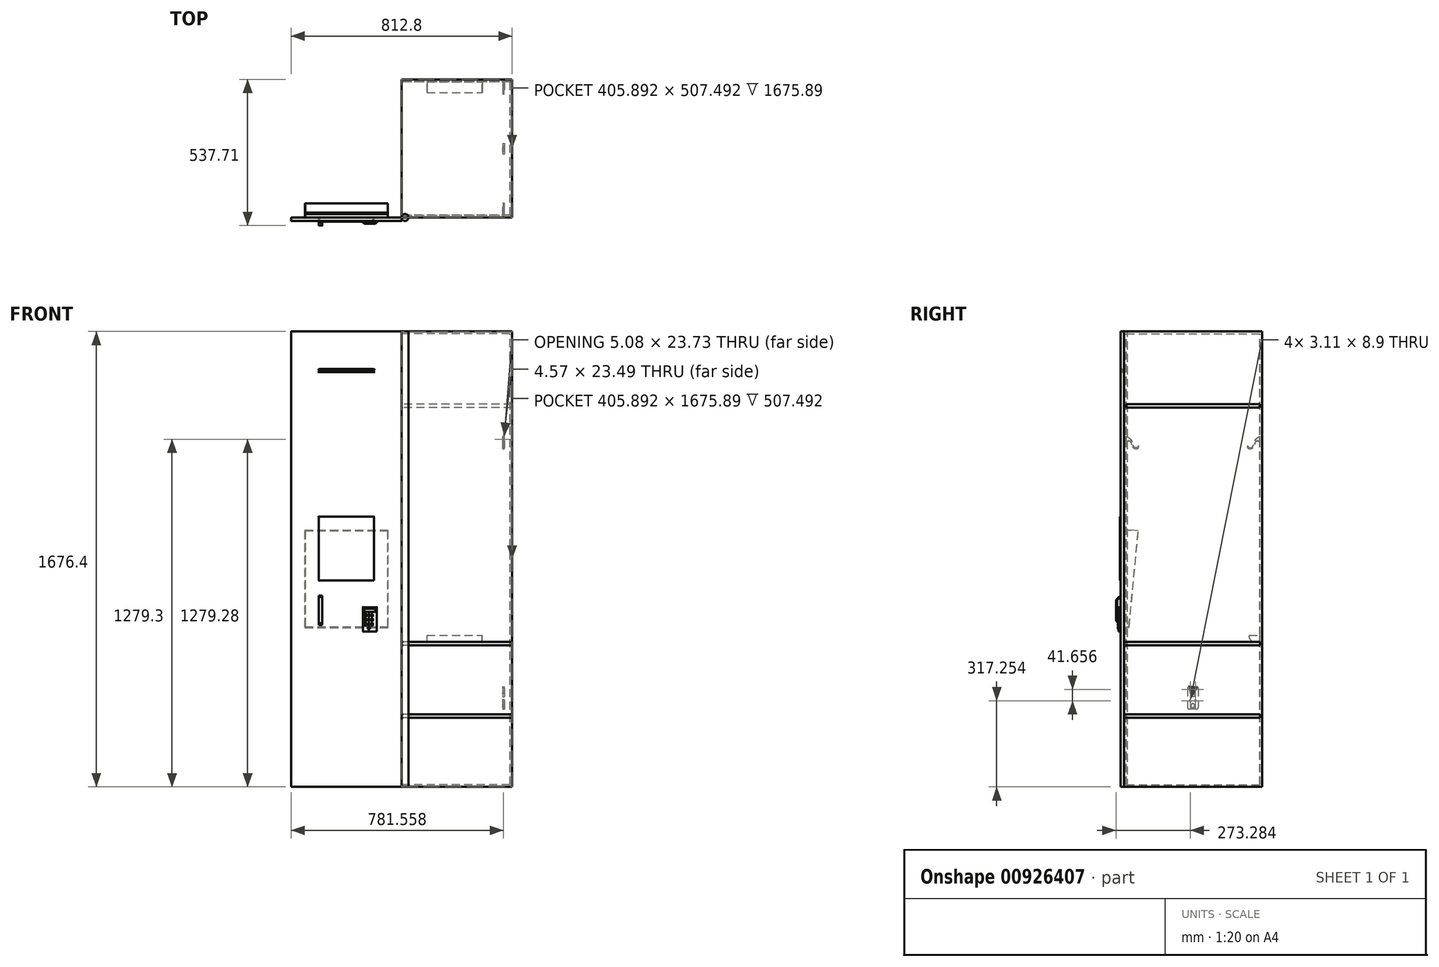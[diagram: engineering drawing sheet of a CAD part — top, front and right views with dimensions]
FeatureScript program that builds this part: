
annotation { "Feature Type Name" : "Feature", "Feature Type Description" : "" }
export const myFeature = defineFeature(function(context is Context, id is Id, definition is map)
    precondition{}
    {
        {
            var Q0;
            Q0=qCreatedBy(makeId("Front.planeOp"),FACE);
            var sketch = newSketch(context, id + "F0", { "sketchPlane" : qUnion([Q0])});
            skLineSegment(sketch, "E0.bottom", {"start": v(0, 0) * mm, "end": v(-406.4, 0) * mm});
            skLineSegment(sketch, "E0.top", {"start": v(0, 1676.4) * mm, "end": v(-406.4, 1676.4) * mm});
            skLineSegment(sketch, "E0.left", {"start": v(0, 0) * mm, "end": v(0, 1676.4) * mm});
            skLineSegment(sketch, "E0.right", {"start": v(-406.4, 0) * mm, "end": v(-406.4, 1676.4) * mm});
            skLineSegment(sketch, "E1.bottom", {"start": v(0, 1676.4) * mm, "end": v(12.7, 1676.4) * mm});
            skLineSegment(sketch, "E1.top", {"start": v(0, 0) * mm, "end": v(12.7, 0) * mm});
            skLineSegment(sketch, "E1.left", {"start": v(0, 1676.4) * mm, "end": v(0, 0) * mm});
            skLineSegment(sketch, "E1.right", {"start": v(12.7, 1676.4) * mm, "end": v(12.7, 0) * mm});
            skLineSegment(sketch, "E2", {"start": v(-406.4, 0) * mm, "end": v(-406.4, 838.2) * mm, "construction": true});
            skLineSegment(sketch, "E3", {"start": v(-406.4, 838.2) * mm, "end": v(-406.4, 1257.3) * mm, "construction": true});
            skLineSegment(sketch, "E4", {"start": v(-406.4, 838.2) * mm, "end": v(-406.4, 1047.75) * mm, "construction": true});
            skLineSegment(sketch, "E5", {"start": v(-406.4, 838.2) * mm, "end": v(-406.4, 628.65) * mm, "construction": true});
            skLineSegment(sketch, "E6", {"start": v(-406.4, 1047.75) * mm, "end": v(0, 1047.75) * mm, "construction": true});
            skLineSegment(sketch, "E7", {"start": v(0, 1047.75) * mm, "end": v(-203.2, 1047.75) * mm, "construction": true});
            skLineSegment(sketch, "E8", {"start": v(-203.2, 1047.75) * mm, "end": v(-101.6, 1047.75) * mm, "construction": true});
            skLineSegment(sketch, "E9", {"start": v(-101.6, 1047.75) * mm, "end": v(-304.8, 1047.75) * mm, "construction": true});
            skLineSegment(sketch, "E10", {"start": v(-406.4, 942.98) * mm, "end": v(-406.4, 838.2) * mm});
            skLineSegment(sketch, "E11", {"start": v(-406.4, 942.98) * mm, "end": v(-406.4, 1047.75) * mm});
            skLineSegment(sketch, "E12", {"start": v(-406.4, 995.36) * mm, "end": v(-406.4, 890.59) * mm});
            skLineSegment(sketch, "E13", {"start": v(-305.48, 995.36) * mm, "end": v(-305.48, 760.41) * mm});
            skLineSegment(sketch, "E14.bottom", {"start": v(-305.48, 995.36) * mm, "end": v(-102.28, 995.36) * mm});
            skLineSegment(sketch, "E14.top", {"start": v(-305.48, 760.41) * mm, "end": v(-102.28, 760.41) * mm});
            skLineSegment(sketch, "E14.right", {"start": v(-102.28, 995.36) * mm, "end": v(-102.28, 760.41) * mm});
            skSolve(sketch);
        }
        {
            var Q0;
            {var subQ2=sQuery(id+"F0.wireOp",EDGE,"E0.bottom");Q0=makeQuery(id+"F0.imprint","IMPRINT",FACE,{"disambiguationData":[TD([[makeQuery(id+"F0.imprint","IMPRINT",EDGE,{"derivedFrom":subQ2}),-1.0]])]});}
            extrude(context, id + "F1", {"entities" : qUnion([Q0]), "depth" : 12.7 * mm, "offsetDistance" : 25.4 * mm});
        }
        {
            var Q0;
            Q0=makeQuery(id+"F0.imprint","IMPRINT",FACE,{"disambiguationData":[TD([[makeQuery(id+"F0.imprint","IMPRINT",EDGE,{"derivedFrom":sQuery(id+"F0.wireOp",EDGE,"E14.bottom")}),-1.0]])]});
            extrude(context, id + "F2", {"entities" : qUnion([Q0]), "operationType" : NewBodyOperationType.ADD, "depth" : 15.24 * mm, "offsetDistance" : 25.4 * mm});
        }
        {
            var Q0;
            Q0=qCreatedBy(makeId("Front.planeOp"),FACE);
            var sketch = newSketch(context, id + "F3", { "sketchPlane" : qUnion([Q0])});
            skLineSegment(sketch, "E15", {"start": v(-406.3, 1483.15) * mm, "end": v(0, 1483.15) * mm, "construction": true});
            skLineSegment(sketch, "E16", {"start": v(-203.15, 1483.15) * mm, "end": v(-406.3, 1483.15) * mm, "construction": true});
            skLineSegment(sketch, "E17", {"start": v(-304.72, 1483.15) * mm, "end": v(-406.3, 1483.15) * mm, "construction": true});
            skLineSegment(sketch, "E18", {"start": v(-203.15, 1483.15) * mm, "end": v(0, 1483.15) * mm, "construction": true});
            skLineSegment(sketch, "E19", {"start": v(-101.57, 1483.15) * mm, "end": v(-203.15, 1483.15) * mm, "construction": true});
            skLineSegment(sketch, "E20", {"start": v(-304.72, 1483.15) * mm, "end": v(-304.72, 1606.16) * mm, "construction": true});
            skLineSegment(sketch, "E21", {"start": v(-203.15, 1483.15) * mm, "end": v(-203.15, 1602.3) * mm, "construction": true});
            skLineSegment(sketch, "E22", {"start": v(-101.57, 1483.15) * mm, "end": v(-101.57, 1609.48) * mm, "construction": true});
            skLineSegment(sketch, "E23", {"start": v(-304.72, 1527.65) * mm, "end": v(-101.57, 1527.65) * mm});
            skLineSegment(sketch, "E24", {"start": v(-101.57, 1527.65) * mm, "end": v(-105.25, 1529.31) * mm});
            skLineSegment(sketch, "E25", {"start": v(-105.25, 1529.31) * mm, "end": v(-203.15, 1529.31) * mm});
            skLineSegment(sketch, "E26", {"start": v(-101.57, 1532.4) * mm, "end": v(-203.15, 1532.4) * mm});
            skLineSegment(sketch, "E27", {"start": v(-101.57, 1532.4) * mm, "end": v(-105.34, 1534.19) * mm});
            skLineSegment(sketch, "E28", {"start": v(-105.34, 1534.19) * mm, "end": v(-203.15, 1534.19) * mm});
            skLineSegment(sketch, "E29", {"start": v(-101.57, 1537.04) * mm, "end": v(-203.15, 1537.04) * mm});
            skLineSegment(sketch, "E30", {"start": v(-101.57, 1537.04) * mm, "end": v(-105.29, 1539) * mm});
            skLineSegment(sketch, "E31", {"start": v(-105.29, 1539) * mm, "end": v(-203.15, 1539) * mm});
            skLineSegment(sketch, "E32.MirrorCS", {"start": v(-301.01, 1539) * mm, "end": v(-203.15, 1539) * mm});
            skLineSegment(sketch, "E33.MirrorCS", {"start": v(-304.72, 1537.04) * mm, "end": v(-203.15, 1537.04) * mm});
            skLineSegment(sketch, "E34.MirrorCS", {"start": v(-300.96, 1534.19) * mm, "end": v(-203.15, 1534.19) * mm});
            skLineSegment(sketch, "E35.MirrorCS", {"start": v(-304.72, 1532.4) * mm, "end": v(-203.15, 1532.4) * mm});
            skLineSegment(sketch, "E36.MirrorCS", {"start": v(-301.05, 1529.31) * mm, "end": v(-203.15, 1529.31) * mm});
            skLineSegment(sketch, "E37.MirrorCS", {"start": v(-101.57, 1527.65) * mm, "end": v(-304.72, 1527.65) * mm});
            skLineSegment(sketch, "E38.MirrorCS", {"start": v(-304.72, 1537.04) * mm, "end": v(-301.01, 1539) * mm});
            skLineSegment(sketch, "E39.MirrorCS", {"start": v(-304.72, 1532.4) * mm, "end": v(-300.96, 1534.19) * mm});
            skLineSegment(sketch, "E40.MirrorCS", {"start": v(-304.72, 1527.65) * mm, "end": v(-301.05, 1529.31) * mm});
            skSolve(sketch);
        }
        {
            var Q0;
            Q0=makeQuery(id+"F3.imprint","IMPRINT",FACE,{"disambiguationData":[TD([[makeQuery(id+"F3.imprint","IMPRINT",EDGE,{"derivedFrom":sQuery(id+"F3.wireOp",EDGE,"E29")}),-1.0]])]});
            var Q1;
            Q1=makeQuery(id+"F3.imprint","IMPRINT",FACE,{"disambiguationData":[TD([[makeQuery(id+"F3.imprint","IMPRINT",EDGE,{"derivedFrom":sQuery(id+"F3.wireOp",EDGE,"E26")}),-1.0]])]});
            var Q2;
            Q2=makeQuery(id+"F3.imprint","IMPRINT",FACE,{"disambiguationData":[TD([[makeQuery(id+"F3.imprint","IMPRINT",EDGE,{"derivedFrom":sQuery(id+"F3.wireOp",EDGE,"E24")}),1.0]])]});
            extrude(context, id + "F4", {"entities" : qUnion([Q0, Q1, Q2]), "operationType" : NewBodyOperationType.REMOVE, "depth" : 12.7 * mm, "offsetDistance" : 25.4 * mm});
        }
        {
            var Q0;
            Q0=makeQuery(id+"F0.imprint","IMPRINT",FACE,{"disambiguationData":[TD([[makeQuery(id+"F0.imprint","IMPRINT",EDGE,{"derivedFrom":sQuery(id+"F0.wireOp",EDGE,"E1.bottom")}),-1.0]])]});
            var Q1;
            Q1=sQuery(id+"F0.wireOp",EDGE,"E1.right");
            revolve(context, id + "F5", {"operationType" : NewBodyOperationType.ADD, "surfaceOperationType" : NewSurfaceOperationType.NEW, "entities" : qUnion([Q0]), "axis" : qUnion([Q1]), "revolveType" : RevolveType.FULL});
        }
        {
            var Q0;
            Q0=qCreatedBy(makeId("Right.planeOp"),FACE);
            cPlane(context, id + "F6", {"entities" : qUnion([Q0]), "cplaneType" : CPlaneType.OFFSET, "offset" : 304.8 * mm, "oppositeDirection" : true, "width" : 152.4 * mm, "height" : 152.4 * mm});
        }
        {
            var Q0;
            Q0=qCreatedBy(id+"F6.planeOp",FACE);
            var sketch = newSketch(context, id + "F7", { "sketchPlane" : qUnion([Q0])});
            skLineSegment(sketch, "E41", {"start": v(-12.56, 688.19) * mm, "end": v(-25.26, 688.19) * mm, "construction": true});
            skLineSegment(sketch, "E42", {"start": v(-12.56, 688.19) * mm, "end": v(-12.56, 611.99) * mm, "construction": true});
            skLineSegment(sketch, "E43", {"start": v(-12.56, 611.99) * mm, "end": v(-25.26, 611.99) * mm, "construction": true});
            skLineSegment(sketch, "E44", {"start": v(-25.26, 685.53) * mm, "end": v(-25.26, 614.48) * mm});
            skLineSegment(sketch, "E45", {"start": v(-23.56, 610.16) * mm, "end": v(-19.06, 605.31) * mm});
            skLineSegment(sketch, "E46", {"start": v(-23.37, 690.05) * mm, "end": v(-18.95, 694.4) * mm});
            skLineSegment(sketch, "E47", {"start": v(-19.06, 605.31) * mm, "end": v(-19.06, 600.87) * mm});
            skLineSegment(sketch, "E48", {"start": v(-18.95, 694.4) * mm, "end": v(-18.95, 698.85) * mm});
            skLineSegment(sketch, "E49", {"start": v(-25.26, 688.19) * mm, "end": v(-29.7, 688.19) * mm, "construction": true});
            skLineSegment(sketch, "E50", {"start": v(-25.26, 611.99) * mm, "end": v(-29.7, 611.99) * mm, "construction": true});
            skLineSegment(sketch, "E51", {"start": v(-29.7, 685.54) * mm, "end": v(-29.7, 614.54) * mm});
            skLineSegment(sketch, "E52", {"start": v(-19.06, 600.87) * mm, "end": v(-27.94, 610.15) * mm});
            skLineSegment(sketch, "E53", {"start": v(-18.95, 698.85) * mm, "end": v(-27.83, 690.05) * mm});
            skPoint(sketch, "E54.visualSharp", {"position": v(-29.7, 688.19) * mm});
            skArc(sketch, "E54.filletArc", {"start": v(-27.83, 690.05) * mm, "mid": v(-29.22, 687.98) * mm, "end": v(-29.7, 685.54) * mm});
            skPoint(sketch, "E55.visualSharp", {"position": v(-29.7, 611.99) * mm});
            skArc(sketch, "E55.filletArc", {"start": v(-29.7, 614.54) * mm, "mid": v(-29.25, 612.17) * mm, "end": v(-27.94, 610.15) * mm});
            skPoint(sketch, "E56.visualSharp", {"position": v(-25.26, 688.19) * mm});
            skArc(sketch, "E56.filletArc", {"start": v(-23.37, 690.05) * mm, "mid": v(-24.77, 687.98) * mm, "end": v(-25.26, 685.53) * mm});
            skPoint(sketch, "E57.visualSharp", {"position": v(-25.26, 611.99) * mm});
            skArc(sketch, "E57.filletArc", {"start": v(-25.26, 614.48) * mm, "mid": v(-24.82, 612.16) * mm, "end": v(-23.56, 610.16) * mm});
            skLineSegment(sketch, "E58", {"start": v(-18.95, 694.4) * mm, "end": v(-12.7, 700.5) * mm});
            skLineSegment(sketch, "E59", {"start": v(-12.7, 700.5) * mm, "end": v(-12.7, 703.47) * mm});
            skLineSegment(sketch, "E60", {"start": v(-12.7, 703.47) * mm, "end": v(-18.95, 698.85) * mm});
            skLineSegment(sketch, "E61", {"start": v(-29.7, 650.04) * mm, "end": v(-12.56, 650.04) * mm, "construction": true});
            skLineSegment(sketch, "E62.MirrorCS", {"start": v(-12.7, 599.57) * mm, "end": v(-12.7, 596.6) * mm});
            skLineSegment(sketch, "E63", {"start": v(-19.06, 600.87) * mm, "end": v(-12.7, 596.6) * mm});
            skLineSegment(sketch, "E64", {"start": v(-12.7, 599.57) * mm, "end": v(-19.06, 605.31) * mm});
            skSolve(sketch);
        }
        {
            var Q0;
            Q0 = qSketchRegion(id + "F7", true);
            extrude(context, id + "F8", {"entities" : qUnion([Q0]), "operationType" : NewBodyOperationType.ADD, "depth" : 12.7 * mm, "offsetDistance" : 25.4 * mm});
        }
        {
            var Q0;
            Q0=makeQuery(id+"F1.opExtrude","CAP_FACE",FACE,{"disambiguationData":[OSD([sQuery(id+"F0.wireOp",EDGE,"E0.bottom"),sQuery(id+"F0.wireOp",EDGE,"E0.top"),sQuery(id+"F0.wireOp",EDGE,"E0.right"),sQuery(id+"F0.wireOp",EDGE,"E1.left"),sQuery(id+"F0.wireOp",EDGE,"E10"),sQuery(id+"F0.wireOp",EDGE,"E11"),sQuery(id+"F0.wireOp",EDGE,"E12"),sQuery(id+"F0.wireOp",EDGE,"E14.bottom"),sQuery(id+"F0.wireOp",EDGE,"E14.top"),sQuery(id+"F0.wireOp",EDGE,"E13"),sQuery(id+"F0.wireOp",EDGE,"E14.right")])],"isStart":false});
            var sketch = newSketch(context, id + "F9", { "sketchPlane" : qUnion([Q0])});
            skLineSegment(sketch, "E65.bottom", {"start": v(-142.47, 661.15) * mm, "end": v(-91.67, 661.15) * mm});
            skLineSegment(sketch, "E65.top", {"start": v(-142.47, 572.25) * mm, "end": v(-91.67, 572.25) * mm});
            skLineSegment(sketch, "E65.left", {"start": v(-142.47, 661.15) * mm, "end": v(-142.47, 572.25) * mm});
            skLineSegment(sketch, "E65.right", {"start": v(-91.67, 661.15) * mm, "end": v(-91.67, 572.25) * mm});
            skSolve(sketch);
        }
        {
            var Q0;
            Q0=makeQuery(id+"F9.imprint","IMPRINT",FACE,{"disambiguationData":[TD([[makeQuery(id+"F9.imprint","IMPRINT",EDGE,{"derivedFrom":sQuery(id+"F9.wireOp",EDGE,"E65.bottom")}),-1.0]])]});
            extrude(context, id + "F10", {"entities" : qUnion([Q0]), "operationType" : NewBodyOperationType.ADD, "depth" : 7.62 * mm, "offsetDistance" : 25.4 * mm});
        }
        {
            var Q0;
            Q0=qCreatedBy(makeId("Right.planeOp"),FACE);
            var sketch = newSketch(context, id + "F11", { "sketchPlane" : qUnion([Q0])});
            skLineSegment(sketch, "E66", {"start": v(0, 944.75) * mm, "end": v(0, 589.15) * mm});
            skLineSegment(sketch, "E67", {"start": v(0, 589.15) * mm, "end": v(12.56, 589.15) * mm, "construction": true});
            skArc(sketch, "E68", {"start": v(0, 589.15) * mm, "mid": v(6.28, 585.93) * mm, "end": v(12.56, 589.15) * mm});
            skLineSegment(sketch, "E69", {"start": v(0, 944.75) * mm, "end": v(25.4, 944.75) * mm});
            skLineSegment(sketch, "E70", {"start": v(25.4, 944.75) * mm, "end": v(12.56, 589.15) * mm});
            skLineSegment(sketch, "E71", {"start": v(12.56, 589.15) * mm, "end": v(18.44, 588.46) * mm, "construction": true});
            skArc(sketch, "E72", {"start": v(12.56, 589.15) * mm, "mid": v(15.34, 587.43) * mm, "end": v(18.44, 588.46) * mm});
            skLineSegment(sketch, "E73", {"start": v(18.44, 588.46) * mm, "end": v(52.56, 943.4) * mm});
            skLineSegment(sketch, "E74", {"start": v(52.56, 943.4) * mm, "end": v(25.4, 944.75) * mm});
            skSolve(sketch);
        }
        {
            var Q0;
            Q0=makeQuery(id+"F11.imprint","IMPRINT",FACE,{"disambiguationData":[TD([[makeQuery(id+"F11.imprint","IMPRINT",EDGE,{"derivedFrom":sQuery(id+"F11.wireOp",EDGE,"E66")}),1.0]])]});
            var Q1;
            Q1=makeQuery(id+"F11.imprint","IMPRINT",FACE,{"disambiguationData":[TD([[makeQuery(id+"F11.imprint","IMPRINT",EDGE,{"derivedFrom":sQuery(id+"F11.wireOp",EDGE,"E70")}),1.0]])]});
            extrude(context, id + "F12", {"entities" : qUnion([Q0, Q1]), "oppositeDirection" : true, "depth" : 355.6 * mm, "offsetDistance" : 25.4 * mm, "hasSecondDirection" : true, "secondDirectionOppositeDirection" : true, "secondDirectionDepth" : 50.8 * mm});
        }
        {
            var Q0;
            Q0=makeQuery(id+"F12.opExtrude","SWEPT_FACE",FACE,{"disambiguationData":[OSD([sQuery(id+"F11.wireOp",EDGE,"E69")])]});
            var Q1;
            Q1=makeQuery(id+"F12.opExtrude","SWEPT_FACE",FACE,{"disambiguationData":[OSD([sQuery(id+"F11.wireOp",EDGE,"E74")])]});
            shell(context, id + "F13", {"entities" : qUnion([Q0, Q1]), "thickness" : 0.5 * mm});
        }
        {
            var Q0;
            Q0=qCreatedBy(id+"F6.planeOp",FACE);
            cPlane(context, id + "F14", {"entities" : qUnion([Q0]), "cplaneType" : CPlaneType.OFFSET, "offset" : 304.8 * mm, "width" : 152.4 * mm, "height" : 152.4 * mm});
        }
        {
            var Q0;
            Q0=qCreatedBy(id+"F14.planeOp",FACE);
            var sketch = newSketch(context, id + "F15", { "sketchPlane" : qUnion([Q0])});
            skLineSegment(sketch, "E75.bottom", {"start": v(0, 0) * mm, "end": v(508, 0) * mm});
            skLineSegment(sketch, "E75.top", {"start": v(0, 1676.4) * mm, "end": v(508, 1676.4) * mm});
            skLineSegment(sketch, "E75.left", {"start": v(0, 0) * mm, "end": v(0, 1676.4) * mm});
            skLineSegment(sketch, "E75.right", {"start": v(508, 0) * mm, "end": v(508, 1676.4) * mm});
            skSolve(sketch);
        }
        {
            var Q0;
            Q0=makeQuery(id+"F15.imprint","IMPRINT",FACE,{"disambiguationData":[TD([[makeQuery(id+"F15.imprint","IMPRINT",EDGE,{"derivedFrom":sQuery(id+"F15.wireOp",EDGE,"E75.bottom")}),1.0]])]});
            extrude(context, id + "F16", {"entities" : qUnion([Q0]), "depth" : 406.4 * mm, "offsetDistance" : 25.4 * mm});
        }
        {
            var Q0;
            Q0=makeQuery(id+"F16.opExtrude","CAP_FACE",FACE,{"disambiguationData":[OSD([sQuery(id+"F15.wireOp",EDGE,"E75.bottom"),sQuery(id+"F15.wireOp",EDGE,"E75.top"),sQuery(id+"F15.wireOp",EDGE,"E75.left"),sQuery(id+"F15.wireOp",EDGE,"E75.right")])],"isStart":true});
            shell(context, id + "F17", {"entities" : qUnion([Q0]), "thickness" : 8.38 * mm});
        }
        {
            var Q0;
            Q0=qCreatedBy(makeId("Right.planeOp"),FACE);
            var sketch = newSketch(context, id + "F18", { "sketchPlane" : qUnion([Q0])});
            skLineSegment(sketch, "E76", {"start": v(0, 0) * mm, "end": v(0, 254) * mm, "construction": true});
            skLineSegment(sketch, "E77.bottom", {"start": v(0, 254) * mm, "end": v(499.7, 254) * mm});
            skLineSegment(sketch, "E77.top", {"start": v(0, 266.7) * mm, "end": v(499.7, 266.7) * mm});
            skLineSegment(sketch, "E77.left", {"start": v(0, 254) * mm, "end": v(0, 266.7) * mm});
            skLineSegment(sketch, "E77.right", {"start": v(499.7, 254) * mm, "end": v(499.7, 266.7) * mm});
            skLineSegment(sketch, "E78", {"start": v(499.52, 1662.87) * mm, "end": v(499.52, 1408.87) * mm});
            skLineSegment(sketch, "E79", {"start": v(499.52, 1408.87) * mm, "end": v(8.06, 1408.87) * mm});
            skLineSegment(sketch, "E80", {"start": v(8.06, 1408.87) * mm, "end": v(8.06, 1396.17) * mm});
            skLineSegment(sketch, "E81.bottom", {"start": v(8.06, 1396.17) * mm, "end": v(499.52, 1396.17) * mm});
            skLineSegment(sketch, "E81.top", {"start": v(8.06, 1408.87) * mm, "end": v(499.52, 1408.87) * mm});
            skLineSegment(sketch, "E81.left", {"start": v(8.06, 1396.17) * mm, "end": v(8.06, 1408.87) * mm});
            skLineSegment(sketch, "E81.right", {"start": v(499.52, 1396.17) * mm, "end": v(499.52, 1408.87) * mm});
            skLineSegment(sketch, "E82", {"start": v(499.7, 266.7) * mm, "end": v(499.7, 520.7) * mm, "construction": true});
            skLineSegment(sketch, "E83.bottom", {"start": v(499.7, 520.7) * mm, "end": v(0, 520.7) * mm});
            skLineSegment(sketch, "E83.top", {"start": v(499.7, 533.4) * mm, "end": v(0, 533.4) * mm});
            skLineSegment(sketch, "E83.left", {"start": v(499.7, 520.7) * mm, "end": v(499.7, 533.4) * mm});
            skLineSegment(sketch, "E83.right", {"start": v(0, 520.7) * mm, "end": v(0, 533.4) * mm});
            skSolve(sketch);
        }
        {
            var Q0;
            Q0=makeQuery(id+"F18.imprint","IMPRINT",FACE,{"disambiguationData":[TD([[makeQuery(id+"F18.imprint","IMPRINT",EDGE,{"derivedFrom":sQuery(id+"F18.wireOp",EDGE,"E77.bottom")}),1.0]])]});
            var Q1;
            Q1=makeQuery(id+"F18.imprint","IMPRINT",FACE,{"disambiguationData":[TD([[makeQuery(id+"F18.imprint","IMPRINT",EDGE,{"derivedFrom":sQuery(id+"F18.wireOp",EDGE,"E81.bottom")}),1.0]])]});
            var Q2;
            Q2=makeQuery(id+"F18.imprint","IMPRINT",FACE,{"disambiguationData":[TD([[makeQuery(id+"F18.imprint","IMPRINT",EDGE,{"derivedFrom":sQuery(id+"F18.wireOp",EDGE,"E83.bottom")}),-1.0]])]});
            extrude(context, id + "F19", {"entities" : qUnion([Q0, Q1, Q2]), "depth" : 406.4 * mm, "offsetDistance" : 25.4 * mm});
        }
        {
            var Q0;
            Q0=makeQuery(id+"F17.opShell","OFFSET_FACE",FACE,{"disambiguationData":[OSD([sQuery(id+"F15.wireOp",EDGE,"E75.bottom"),sQuery(id+"F15.wireOp",EDGE,"E75.top"),sQuery(id+"F15.wireOp",EDGE,"E75.left"),sQuery(id+"F15.wireOp",EDGE,"E75.right")])]});
            var sketch = newSketch(context, id + "F20", { "sketchPlane" : qUnion([Q0])});
            skFitSpline(sketch, "E84", {"points": [v(-8.38, 1267.43) * mm, v(-14.6, 1272.52) * mm, v(-21.72, 1272.52) * mm, v(-26.81, 1261.33) * mm, v(-33.6, 1247.77) * mm, v(-50.88, 1245.74) * mm, v(-53.25, 1256.24) * mm], "startDerivative": vector(-40.68, 42.62) * mm, "endDerivative": vector(4.88, 79.27) * mm});
            skFitSpline(sketch, "E85", {"points": [v(-53.25, 1256.24) * mm, v(-48.17, 1249.46) * mm, v(-37.32, 1250.82) * mm, v(-31.22, 1262.69) * mm, v(-26.13, 1277.26) * mm, v(-8.38, 1291.16) * mm], "startDerivative": vector(23.62, -52.78) * mm, "endDerivative": vector(82.29, 50.25) * mm});
            skLineSegment(sketch, "E86", {"start": v(-8.38, 1291.16) * mm, "end": v(-8.38, 1267.43) * mm});
            skLineSegment(sketch, "E87", {"start": v(-8.38, 1291.16) * mm, "end": v(-499.62, 1291.16) * mm, "construction": true});
            skLineSegment(sketch, "E88", {"start": v(-499.62, 1291.16) * mm, "end": v(-254, 1291.16) * mm, "construction": true});
            skLineSegment(sketch, "E89", {"start": v(-254, 1291.16) * mm, "end": v(-254, 1202) * mm, "construction": true});
            skFitSpline(sketch, "E90.MirrorCS", {"points": [v(-454.75, 1256.24) * mm, v(-459.83, 1249.46) * mm, v(-470.68, 1250.82) * mm, v(-476.78, 1262.69) * mm, v(-481.87, 1277.26) * mm, v(-499.62, 1291.16) * mm], "startDerivative": vector(-23.62, -52.78) * mm, "endDerivative": vector(-82.29, 50.25) * mm});
            skFitSpline(sketch, "E91.MirrorCS", {"points": [v(-499.62, 1267.43) * mm, v(-493.4, 1272.52) * mm, v(-486.28, 1272.52) * mm, v(-481.19, 1261.33) * mm, v(-474.4, 1247.77) * mm, v(-457.12, 1245.74) * mm, v(-454.75, 1256.24) * mm], "startDerivative": vector(40.68, 42.62) * mm, "endDerivative": vector(-4.88, 79.27) * mm});
            skLineSegment(sketch, "E92.MirrorCS", {"start": v(-499.62, 1291.16) * mm, "end": v(-499.62, 1267.43) * mm});
            skLineSegment(sketch, "E93", {"start": v(-499.62, 327.67) * mm, "end": v(-8.38, 327.67) * mm, "construction": true});
            skLineSegment(sketch, "E94", {"start": v(-8.38, 327.67) * mm, "end": v(-253.3, 327.67) * mm, "construction": true});
            skLineSegment(sketch, "E95.bottom", {"start": v(-266.37, 369.32) * mm, "end": v(-240.2, 369.32) * mm});
            skLineSegment(sketch, "E95.top", {"start": v(-266.37, 286.01) * mm, "end": v(-240.2, 286.01) * mm});
            skLineSegment(sketch, "E95.left", {"start": v(-272.72, 362.97) * mm, "end": v(-272.72, 292.36) * mm});
            skLineSegment(sketch, "E95.right", {"start": v(-233.86, 362.97) * mm, "end": v(-233.86, 292.36) * mm});
            skPoint(sketch, "E95.middle", {"position": v(-253.3, 327.67) * mm});
            skLineSegment(sketch, "E96", {"start": v(-253.3, 327.67) * mm, "end": v(-253.3, 369.32) * mm, "construction": true});
            skLineSegment(sketch, "E97", {"start": v(-253.3, 369.32) * mm, "end": v(-272.72, 369.32) * mm, "construction": true});
            skLineSegment(sketch, "E98", {"start": v(-263, 369.32) * mm, "end": v(-263, 327.67) * mm, "construction": true});
            skLineSegment(sketch, "E99", {"start": v(-253.3, 327.67) * mm, "end": v(-233.86, 327.67) * mm, "construction": true});
            skLineSegment(sketch, "E100", {"start": v(-233.86, 327.67) * mm, "end": v(-243.57, 327.67) * mm, "construction": true});
            skLineSegment(sketch, "E101", {"start": v(-243.57, 327.67) * mm, "end": v(-243.57, 369.32) * mm, "construction": true});
            skLineSegment(sketch, "E102", {"start": v(-233.86, 327.67) * mm, "end": v(-233.86, 369.32) * mm, "construction": true});
            skLineSegment(sketch, "E103", {"start": v(-233.86, 348.5) * mm, "end": v(-272.72, 348.5) * mm, "construction": true});
            skLineSegment(sketch, "E104", {"start": v(-272.72, 348.5) * mm, "end": v(-272.72, 369.32) * mm, "construction": true});
            skLineSegment(sketch, "E105", {"start": v(-272.72, 358.91) * mm, "end": v(-233.86, 358.91) * mm, "construction": true});
            skLineSegment(sketch, "E106", {"start": v(-233.86, 358.91) * mm, "end": v(-233.86, 327.67) * mm, "construction": true});
            skLineSegment(sketch, "E107", {"start": v(-233.86, 327.67) * mm, "end": v(-233.86, 348.5) * mm, "construction": true});
            skLineSegment(sketch, "E108", {"start": v(-233.86, 338.08) * mm, "end": v(-272.72, 338.08) * mm, "construction": true});
            skLineSegment(sketch, "E109.MirrorCS", {"start": v(-263, 286.01) * mm, "end": v(-263, 327.67) * mm, "construction": true});
            skLineSegment(sketch, "E110.MirrorCS", {"start": v(-253.3, 327.67) * mm, "end": v(-253.3, 286.01) * mm, "construction": true});
            skLineSegment(sketch, "E111.MirrorCS", {"start": v(-243.57, 327.67) * mm, "end": v(-243.57, 286.01) * mm, "construction": true});
            skLineSegment(sketch, "E112.MirrorCS", {"start": v(-233.86, 317.25) * mm, "end": v(-272.72, 317.25) * mm, "construction": true});
            skLineSegment(sketch, "E113.MirrorCS", {"start": v(-233.86, 306.84) * mm, "end": v(-272.72, 306.84) * mm, "construction": true});
            skLineSegment(sketch, "E114.MirrorCS", {"start": v(-272.72, 296.43) * mm, "end": v(-233.86, 296.43) * mm, "construction": true});
            skLineSegment(sketch, "E115.bottom", {"start": v(-264.56, 363.36) * mm, "end": v(-261.45, 363.36) * mm});
            skLineSegment(sketch, "E115.top", {"start": v(-264.56, 354.46) * mm, "end": v(-261.45, 354.46) * mm});
            skLineSegment(sketch, "E115.left", {"start": v(-264.56, 363.36) * mm, "end": v(-264.56, 354.46) * mm});
            skLineSegment(sketch, "E115.right", {"start": v(-261.45, 363.36) * mm, "end": v(-261.45, 354.46) * mm});
            skPoint(sketch, "E115.middle", {"position": v(-263, 358.91) * mm});
            skLineSegment(sketch, "E116.MirrorCS", {"start": v(-242.02, 363.36) * mm, "end": v(-242.02, 354.46) * mm});
            skLineSegment(sketch, "E117.MirrorCS", {"start": v(-245.13, 363.36) * mm, "end": v(-245.13, 354.46) * mm});
            skLineSegment(sketch, "E118.MirrorCS", {"start": v(-242.02, 363.36) * mm, "end": v(-245.13, 363.36) * mm});
            skLineSegment(sketch, "E119.MirrorCS", {"start": v(-242.02, 354.46) * mm, "end": v(-245.13, 354.46) * mm});
            skLineSegment(sketch, "E120.MirrorCS", {"start": v(-264.56, 312.8) * mm, "end": v(-264.56, 321.7) * mm});
            skLineSegment(sketch, "E121.MirrorCS", {"start": v(-261.45, 312.8) * mm, "end": v(-261.45, 321.7) * mm});
            skLineSegment(sketch, "E122.MirrorCS", {"start": v(-264.56, 312.8) * mm, "end": v(-261.45, 312.8) * mm});
            skLineSegment(sketch, "E123.MirrorCS", {"start": v(-264.56, 321.7) * mm, "end": v(-261.45, 321.7) * mm});
            skLineSegment(sketch, "E124.MirrorCS", {"start": v(-242.02, 321.7) * mm, "end": v(-245.13, 321.7) * mm});
            skLineSegment(sketch, "E125.MirrorCS", {"start": v(-242.02, 312.8) * mm, "end": v(-242.02, 321.7) * mm});
            skLineSegment(sketch, "E126.MirrorCS", {"start": v(-242.02, 312.8) * mm, "end": v(-245.13, 312.8) * mm});
            skLineSegment(sketch, "E127.MirrorCS", {"start": v(-245.13, 312.8) * mm, "end": v(-245.13, 321.7) * mm});
            skLineSegment(sketch, "E128.bottom", {"start": v(-258.9, 343.8) * mm, "end": v(-247.68, 343.8) * mm});
            skLineSegment(sketch, "E128.top", {"start": v(-258.9, 332.36) * mm, "end": v(-247.68, 332.36) * mm});
            skLineSegment(sketch, "E128.left", {"start": v(-258.9, 343.8) * mm, "end": v(-258.9, 332.36) * mm});
            skLineSegment(sketch, "E128.right", {"start": v(-247.68, 343.8) * mm, "end": v(-247.68, 332.36) * mm});
            skPoint(sketch, "E128.middle", {"position": v(-253.3, 338.08) * mm});
            skLineSegment(sketch, "E129.MirrorCS", {"start": v(-258.9, 302.15) * mm, "end": v(-247.68, 302.15) * mm});
            skLineSegment(sketch, "E130.MirrorCS", {"start": v(-258.9, 290.7) * mm, "end": v(-258.9, 302.15) * mm});
            skLineSegment(sketch, "E131.MirrorCS", {"start": v(-258.9, 290.7) * mm, "end": v(-247.68, 290.7) * mm});
            skLineSegment(sketch, "E132.MirrorCS", {"start": v(-247.68, 290.7) * mm, "end": v(-247.68, 302.15) * mm});
            skArc(sketch, "E133", {"start": v(-247.68, 302.15) * mm, "mid": v(-253.3, 306.79) * mm, "end": v(-258.9, 302.15) * mm});
            skArc(sketch, "E134", {"start": v(-247.68, 343.8) * mm, "mid": v(-253.3, 348.73) * mm, "end": v(-258.9, 343.8) * mm});
            skPoint(sketch, "E135.visualSharp", {"position": v(-272.72, 369.32) * mm});
            skArc(sketch, "E135.filletArc", {"start": v(-266.37, 369.32) * mm, "mid": v(-270.86, 367.46) * mm, "end": v(-272.72, 362.97) * mm});
            skPoint(sketch, "E136.visualSharp", {"position": v(-233.86, 286.01) * mm});
            skArc(sketch, "E136.filletArc", {"start": v(-240.2, 286.01) * mm, "mid": v(-235.72, 287.87) * mm, "end": v(-233.86, 292.36) * mm});
            skPoint(sketch, "E137.visualSharp", {"position": v(-272.72, 286.01) * mm});
            skArc(sketch, "E137.filletArc", {"start": v(-272.72, 292.36) * mm, "mid": v(-270.86, 287.87) * mm, "end": v(-266.37, 286.01) * mm});
            skPoint(sketch, "E138.visualSharp", {"position": v(-233.86, 369.32) * mm});
            skArc(sketch, "E138.filletArc", {"start": v(-233.86, 362.97) * mm, "mid": v(-235.72, 367.46) * mm, "end": v(-240.2, 369.32) * mm});
            skSolve(sketch);
        }
        {
            var Q0;
            Q0 = qSketchRegion(id + "F20", true);
            extrude(context, id + "F21", {"entities" : qUnion([Q0]), "operationType" : NewBodyOperationType.ADD, "depth" : 25.4 * mm, "offsetDistance" : 25.4 * mm, "hasSecondDirection" : true, "secondDirectionOppositeDirection" : false, "secondDirectionDepth" : 20.32 * mm});
        }
        {
            var Q0;
            Q0=makeQuery(id+"F17.opShell","OFFSET_FACE",FACE,{"disambiguationData":[OSD([sQuery(id+"F15.wireOp",EDGE,"E75.bottom"),sQuery(id+"F15.wireOp",EDGE,"E75.top"),sQuery(id+"F15.wireOp",EDGE,"E75.left"),sQuery(id+"F15.wireOp",EDGE,"E75.right")])]});
            var sketch = newSketch(context, id + "F22", { "sketchPlane" : qUnion([Q0])});
            skLineSegment(sketch, "E139", {"start": v(-499.62, 533.78) * mm, "end": v(-486.04, 533.78) * mm});
            skLineSegment(sketch, "E140", {"start": v(-499.62, 549.2) * mm, "end": v(-499.62, 533.78) * mm});
            skLineSegment(sketch, "E141", {"start": v(-486.04, 533.78) * mm, "end": v(-480.99, 533.78) * mm});
            skArc(sketch, "E142", {"start": v(-480.99, 533.78) * mm, "mid": v(-464.94, 541.02) * mm, "end": v(-459.74, 557.84) * mm});
            skLineSegment(sketch, "E143", {"start": v(-459.74, 557.84) * mm, "end": v(-499.62, 557.84) * mm});
            skLineSegment(sketch, "E144", {"start": v(-499.62, 557.84) * mm, "end": v(-499.62, 549.2) * mm});
            skSolve(sketch);
        }
        {
            var Q0;
            Q0 = qSketchRegion(id + "F22", true);
            extrude(context, id + "F23", {"entities" : qUnion([Q0]), "operationType" : NewBodyOperationType.ADD, "depth" : 304.8 * mm, "offsetDistance" : 25.4 * mm, "hasSecondDirection" : true, "secondDirectionOppositeDirection" : false, "secondDirectionDepth" : 101.6 * mm});
        }
        {
            var Q0;
            Q0=makeQuery(id+"F23.opExtrude","SWEPT_FACE",FACE,{"disambiguationData":[OSD([sQuery(id+"F22.wireOp",EDGE,"E143")])]});
            shell(context, id + "F24", {"entities" : qUnion([Q0]), "thickness" : 0.25 * mm});
        }
        {
            var Q0;
            Q0=makeQuery(id+"F19.opExtrude","CAP_EDGE",EDGE,{"disambiguationData":[OSD([sQuery(id+"F18.wireOp",EDGE,"E83.top")])],"isStart":true});
            var Q1;
            Q1=makeQuery(id+"F19.opExtrude","CAP_EDGE",EDGE,{"disambiguationData":[OSD([sQuery(id+"F18.wireOp",EDGE,"E83.bottom")])],"isStart":true});
            var Q2;
            Q2=makeQuery(id+"F19.opExtrude","CAP_EDGE",EDGE,{"disambiguationData":[OSD([sQuery(id+"F18.wireOp",EDGE,"E77.top")])],"isStart":true});
            var Q3;
            Q3=makeQuery(id+"F19.opExtrude","CAP_EDGE",EDGE,{"disambiguationData":[OSD([sQuery(id+"F18.wireOp",EDGE,"E77.bottom")])],"isStart":true});
            var Q4;
            Q4=makeQuery(id+"F19.opExtrude","CAP_EDGE",EDGE,{"disambiguationData":[OSD([sQuery(id+"F18.wireOp",EDGE,"E81.bottom")])],"isStart":true});
            var Q5;
            Q5=makeQuery(id+"F19.opExtrude","CAP_EDGE",EDGE,{"disambiguationData":[OSD([sQuery(id+"F18.wireOp",EDGE,"E81.top")])],"isStart":true});
            fillet(context, id + "F25", {"entities" : qUnion([Q0, Q1, Q2, Q3, Q4, Q5]), "radius" : 5.08 * mm, "tangentPropagation" : true, "allowEdgeOverflow" : false});
        }
        {
            var Q0;
            Q0=makeQuery(id+"F21.opExtrude","CAP_EDGE",EDGE,{"disambiguationData":[OSD([sQuery(id+"F20.wireOp",EDGE,"E85")])],"isStart":false});
            var Q1;
            Q1=makeQuery(id+"F21.opExtrude","CAP_EDGE",EDGE,{"disambiguationData":[OSD([sQuery(id+"F20.wireOp",EDGE,"E84")])],"isStart":true});
            var Q2;
            Q2=makeQuery(id+"F21.opExtrude","CAP_EDGE",EDGE,{"disambiguationData":[OSD([sQuery(id+"F20.wireOp",EDGE,"E84")])],"isStart":false});
            var Q3;
            Q3=makeQuery(id+"F21.opExtrude","CAP_EDGE",EDGE,{"disambiguationData":[OSD([sQuery(id+"F20.wireOp",EDGE,"E85")])],"isStart":true});
            fillet(context, id + "F26", {"entities" : qUnion([Q0, Q1, Q2, Q3]), "radius" : 0.76 * mm, "tangentPropagation" : true, "allowEdgeOverflow" : false});
        }
        {
            var Q0;
            Q0=makeQuery(id+"F1.opExtrude","CAP_FACE",FACE,{"disambiguationData":[OSD([sQuery(id+"F0.wireOp",EDGE,"E0.bottom"),sQuery(id+"F0.wireOp",EDGE,"E0.top"),sQuery(id+"F0.wireOp",EDGE,"E0.right"),sQuery(id+"F0.wireOp",EDGE,"E1.left"),sQuery(id+"F0.wireOp",EDGE,"E10"),sQuery(id+"F0.wireOp",EDGE,"E11"),sQuery(id+"F0.wireOp",EDGE,"E12"),sQuery(id+"F0.wireOp",EDGE,"E14.bottom"),sQuery(id+"F0.wireOp",EDGE,"E14.top"),sQuery(id+"F0.wireOp",EDGE,"E13"),sQuery(id+"F0.wireOp",EDGE,"E14.right")])],"isStart":false});
            var Q1;
            Q1=makeQuery(id+"F21.opExtrude","CAP_EDGE",EDGE,{"disambiguationData":[OSD([sQuery(id+"F20.wireOp",EDGE,"E90.MirrorCS")])],"isStart":true});
            var Q2;
            Q2=makeQuery(id+"F21.opExtrude","CAP_EDGE",EDGE,{"disambiguationData":[OSD([sQuery(id+"F20.wireOp",EDGE,"E90.MirrorCS")])],"isStart":false});
            var Q3;
            Q3=makeQuery(id+"F21.opExtrude","CAP_EDGE",EDGE,{"disambiguationData":[OSD([sQuery(id+"F20.wireOp",EDGE,"E91.MirrorCS")])],"isStart":false});
            var Q4;
            Q4=makeQuery(id+"F21.opExtrude","CAP_EDGE",EDGE,{"disambiguationData":[OSD([sQuery(id+"F20.wireOp",EDGE,"E91.MirrorCS")])],"isStart":true});
            fillet(context, id + "F27", {"entities" : qUnion([Q0, Q1, Q2, Q3, Q4]), "radius" : 0.76 * mm, "tangentPropagation" : true, "allowEdgeOverflow" : false});
        }
        {
            var Q0;
            Q0=makeQuery(id+"F1.opExtrude","CAP_FACE",FACE,{"disambiguationData":[OSD([sQuery(id+"F0.wireOp",EDGE,"E0.bottom"),sQuery(id+"F0.wireOp",EDGE,"E0.top"),sQuery(id+"F0.wireOp",EDGE,"E0.right"),sQuery(id+"F0.wireOp",EDGE,"E1.left"),sQuery(id+"F0.wireOp",EDGE,"E10"),sQuery(id+"F0.wireOp",EDGE,"E11"),sQuery(id+"F0.wireOp",EDGE,"E12"),sQuery(id+"F0.wireOp",EDGE,"E14.bottom"),sQuery(id+"F0.wireOp",EDGE,"E14.top"),sQuery(id+"F0.wireOp",EDGE,"E13"),sQuery(id+"F0.wireOp",EDGE,"E14.right")])],"isStart":false});
            var sketch = newSketch(context, id + "F28", { "sketchPlane" : qUnion([Q0])});
            skLineSegment(sketch, "E145.bottom", {"start": v(-136.75, 655.86) * mm, "end": v(-96.75, 655.86) * mm});
            skLineSegment(sketch, "E145.top", {"start": v(-136.75, 644) * mm, "end": v(-96.75, 644) * mm});
            skLineSegment(sketch, "E145.left", {"start": v(-136.75, 655.86) * mm, "end": v(-136.75, 644) * mm});
            skLineSegment(sketch, "E145.right", {"start": v(-96.75, 655.86) * mm, "end": v(-96.75, 644) * mm});
            skLineSegment(sketch, "E146.bottom", {"start": v(-137.43, 636.2) * mm, "end": v(-128.62, 636.2) * mm});
            skLineSegment(sketch, "E146.top", {"start": v(-137.43, 626.36) * mm, "end": v(-128.62, 626.36) * mm});
            skLineSegment(sketch, "E146.left", {"start": v(-137.43, 636.2) * mm, "end": v(-137.43, 626.36) * mm});
            skLineSegment(sketch, "E146.right", {"start": v(-128.62, 636.2) * mm, "end": v(-128.62, 626.36) * mm});
            skLineSegment(sketch, "E147.bottom", {"start": v(-124.89, 636.2) * mm, "end": v(-116.41, 636.2) * mm});
            skLineSegment(sketch, "E147.top", {"start": v(-124.89, 626.02) * mm, "end": v(-116.41, 626.02) * mm});
            skLineSegment(sketch, "E147.left", {"start": v(-124.89, 636.2) * mm, "end": v(-124.89, 626.02) * mm});
            skLineSegment(sketch, "E147.right", {"start": v(-116.41, 636.2) * mm, "end": v(-116.41, 626.02) * mm});
            skLineSegment(sketch, "E148.bottom", {"start": v(-113.36, 636.11) * mm, "end": v(-105.22, 636.11) * mm});
            skLineSegment(sketch, "E148.top", {"start": v(-113.36, 626.08) * mm, "end": v(-105.22, 626.08) * mm});
            skLineSegment(sketch, "E148.left", {"start": v(-113.36, 636.11) * mm, "end": v(-113.36, 626.08) * mm});
            skLineSegment(sketch, "E148.right", {"start": v(-105.22, 636.11) * mm, "end": v(-105.22, 626.08) * mm});
            skLineSegment(sketch, "E149", {"start": v(-139.8, 622.98) * mm, "end": v(-106.92, 622.98) * mm, "construction": true});
            skLineSegment(sketch, "E150.MirrorCS", {"start": v(-128.62, 609.76) * mm, "end": v(-128.62, 619.59) * mm});
            skLineSegment(sketch, "E151.MirrorCS", {"start": v(-137.43, 619.59) * mm, "end": v(-128.62, 619.59) * mm});
            skLineSegment(sketch, "E152.MirrorCS", {"start": v(-137.43, 609.76) * mm, "end": v(-137.43, 619.59) * mm});
            skLineSegment(sketch, "E153.MirrorCS", {"start": v(-137.43, 609.76) * mm, "end": v(-128.62, 609.76) * mm});
            skLineSegment(sketch, "E154.MirrorCS", {"start": v(-124.89, 609.76) * mm, "end": v(-116.41, 609.76) * mm});
            skLineSegment(sketch, "E155.MirrorCS", {"start": v(-124.89, 609.76) * mm, "end": v(-124.89, 619.93) * mm});
            skLineSegment(sketch, "E156.MirrorCS", {"start": v(-116.41, 609.76) * mm, "end": v(-116.41, 619.93) * mm});
            skLineSegment(sketch, "E157.MirrorCS", {"start": v(-124.89, 619.93) * mm, "end": v(-116.41, 619.93) * mm});
            skLineSegment(sketch, "E158.MirrorCS", {"start": v(-113.36, 619.87) * mm, "end": v(-105.22, 619.87) * mm});
            skLineSegment(sketch, "E159.MirrorCS", {"start": v(-113.36, 609.84) * mm, "end": v(-113.36, 619.87) * mm});
            skLineSegment(sketch, "E160.MirrorCS", {"start": v(-113.36, 609.84) * mm, "end": v(-105.22, 609.84) * mm});
            skLineSegment(sketch, "E161.MirrorCS", {"start": v(-105.22, 609.84) * mm, "end": v(-105.22, 619.87) * mm});
            skLineSegment(sketch, "E162", {"start": v(-139.94, 606.7) * mm, "end": v(-105.02, 606.7) * mm, "construction": true});
            skLineSegment(sketch, "E163.MirrorCS", {"start": v(-113.36, 603.55) * mm, "end": v(-105.22, 603.55) * mm});
            skLineSegment(sketch, "E164.MirrorCS", {"start": v(-113.36, 603.55) * mm, "end": v(-113.36, 593.52) * mm});
            skLineSegment(sketch, "E165.MirrorCS", {"start": v(-113.36, 593.52) * mm, "end": v(-105.22, 593.52) * mm});
            skLineSegment(sketch, "E166.MirrorCS", {"start": v(-105.22, 603.55) * mm, "end": v(-105.22, 593.52) * mm});
            skLineSegment(sketch, "E167.MirrorCS", {"start": v(-116.41, 603.63) * mm, "end": v(-116.41, 593.46) * mm});
            skLineSegment(sketch, "E168.MirrorCS", {"start": v(-124.89, 593.46) * mm, "end": v(-116.41, 593.46) * mm});
            skLineSegment(sketch, "E169.MirrorCS", {"start": v(-124.89, 603.63) * mm, "end": v(-124.89, 593.46) * mm});
            skLineSegment(sketch, "E170.MirrorCS", {"start": v(-124.89, 603.63) * mm, "end": v(-116.41, 603.63) * mm});
            skLineSegment(sketch, "E171.MirrorCS", {"start": v(-128.62, 603.63) * mm, "end": v(-128.62, 593.8) * mm});
            skLineSegment(sketch, "E172.MirrorCS", {"start": v(-137.43, 603.63) * mm, "end": v(-128.62, 603.63) * mm});
            skLineSegment(sketch, "E173.MirrorCS", {"start": v(-137.43, 603.63) * mm, "end": v(-137.43, 593.8) * mm});
            skLineSegment(sketch, "E174.MirrorCS", {"start": v(-137.43, 593.8) * mm, "end": v(-128.62, 593.8) * mm});
            skLineSegment(sketch, "E175.bottom", {"start": v(-125.02, 591.1) * mm, "end": v(-116.71, 591.1) * mm});
            skLineSegment(sketch, "E175.top", {"start": v(-125.02, 581.27) * mm, "end": v(-116.71, 581.27) * mm});
            skLineSegment(sketch, "E175.left", {"start": v(-125.02, 591.1) * mm, "end": v(-125.02, 581.27) * mm});
            skLineSegment(sketch, "E175.right", {"start": v(-116.71, 591.1) * mm, "end": v(-116.71, 581.27) * mm});
            skSolve(sketch);
        }
        {
            var Q0;
            Q0 = qSketchRegion(id + "F28", true);
            extrude(context, id + "F29", {"entities" : qUnion([Q0]), "operationType" : NewBodyOperationType.ADD, "depth" : 10.16 * mm, "offsetDistance" : 25.4 * mm});
        }
    });
